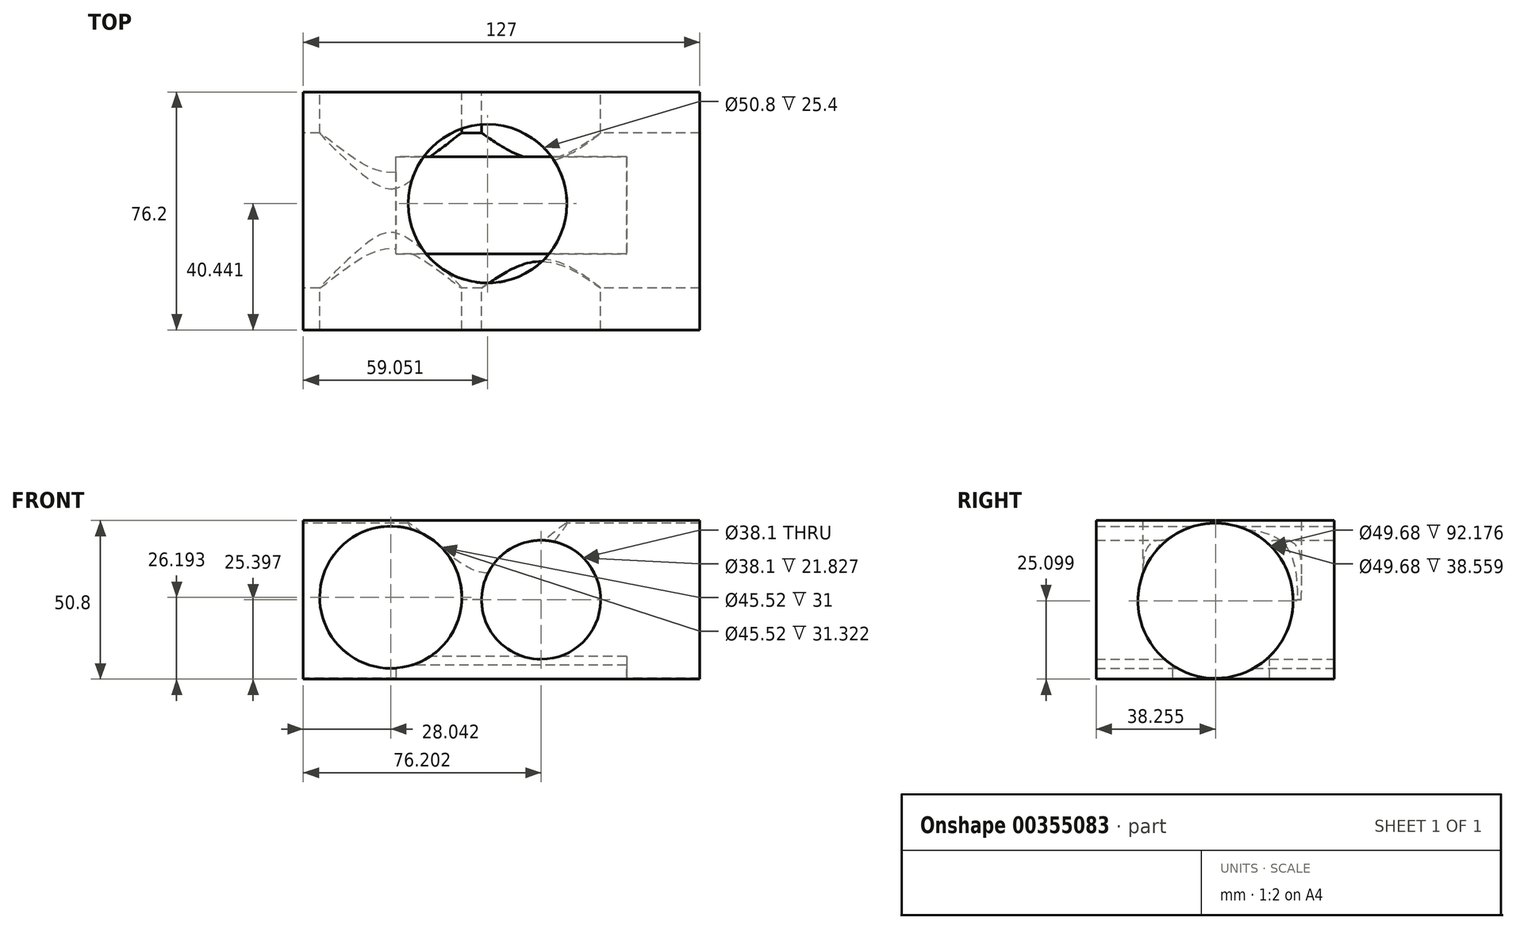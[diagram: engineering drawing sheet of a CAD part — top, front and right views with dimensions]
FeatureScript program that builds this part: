
annotation { "Feature Type Name" : "Feature", "Feature Type Description" : "" }
export const myFeature = defineFeature(function(context is Context, id is Id, definition is map)
    precondition{}
    {
        {
            var Q0;
            Q0=qCreatedBy(makeId("Front.planeOp"),FACE);
            var sketch = newSketch(context, id + "F0", { "sketchPlane" : qUnion([Q0])});
            skLineSegment(sketch, "E0.bottom", {"start": v(-45.49, 55.88) * mm, "end": v(81.51, 55.88) * mm});
            skLineSegment(sketch, "E0.top", {"start": v(-45.49, 5.08) * mm, "end": v(81.51, 5.08) * mm});
            skLineSegment(sketch, "E0.left", {"start": v(-45.49, 55.88) * mm, "end": v(-45.49, 5.08) * mm});
            skLineSegment(sketch, "E0.right", {"start": v(81.51, 55.88) * mm, "end": v(81.51, 5.08) * mm});
            skCircle(sketch, "E1", {"center": v(30.71, 30.48) * mm, "radius": 19.05 * mm});
            skSolve(sketch);
        }
        {
            var Q0;
            Q0=makeQuery(id+"F0.imprint","IMPRINT",FACE,{"disambiguationData":[TD([[makeQuery(id+"F0.imprint","IMPRINT",EDGE,{"derivedFrom":sQuery(id+"F0.wireOp",EDGE,"E0.bottom")}),-1.0]])]});
            extrude(context, id + "F1", {"entities" : qUnion([Q0]), "depth" : 76.2 * mm});
        }
        {
            var Q0;
            Q0=makeQuery(id+"F1.opExtrude","SWEPT_FACE",FACE,{"disambiguationData":[OSD([sQuery(id+"F0.wireOp",EDGE,"E0.bottom")])]});
            var sketch = newSketch(context, id + "F2", { "sketchPlane" : qUnion([Q0])});
            skCircle(sketch, "E2", {"center": v(13.56, -35.76) * mm, "radius": 25.4 * mm});
            skSolve(sketch);
        }
        {
            var Q0;
            Q0=makeQuery(id+"F2.imprint","IMPRINT",FACE,{"disambiguationData":[TD([[makeQuery(id+"F2.imprint","IMPRINT",EDGE,{"derivedFrom":sQuery(id+"F2.wireOp",EDGE,"E2")}),1.0]])]});
            extrude(context, id + "F3", {"entities" : qUnion([Q0]), "operationType" : NewBodyOperationType.REMOVE, "oppositeDirection" : true, "depth" : 25.4 * mm});
        }
        {
            var Q0;
            Q0=makeQuery(id+"F1.opExtrude","SWEPT_FACE",FACE,{"disambiguationData":[OSD([sQuery(id+"F0.wireOp",EDGE,"E0.top")])]});
            var sketch = newSketch(context, id + "F4", { "sketchPlane" : qUnion([Q0])});
            skLineSegment(sketch, "E3.bottom", {"start": v(-15.82, 51.78) * mm, "end": v(58.1, 51.78) * mm});
            skLineSegment(sketch, "E3.top", {"start": v(-15.82, 20.71) * mm, "end": v(58.1, 20.71) * mm});
            skLineSegment(sketch, "E3.left", {"start": v(-15.82, 51.78) * mm, "end": v(-15.82, 20.71) * mm});
            skLineSegment(sketch, "E3.right", {"start": v(58.1, 51.78) * mm, "end": v(58.1, 20.71) * mm});
            skSolve(sketch);
        }
        {
            var Q0;
            Q0=makeQuery(id+"F4.imprint","IMPRINT",FACE,{"disambiguationData":[TD([[makeQuery(id+"F4.imprint","IMPRINT",EDGE,{"derivedFrom":sQuery(id+"F4.wireOp",EDGE,"E3.bottom")}),-1.0]])]});
            extrude(context, id + "F5", {"entities" : qUnion([Q0]), "operationType" : NewBodyOperationType.REMOVE, "oppositeDirection" : true, "depth" : 25.4 * mm});
        }
        {
            var Q0;
            Q0=makeQuery(id+"F1.opExtrude","SWEPT_FACE",FACE,{"disambiguationData":[OSD([sQuery(id+"F0.wireOp",EDGE,"E0.left")])]});
            var sketch = newSketch(context, id + "F6", { "sketchPlane" : qUnion([Q0])});
            skCircle(sketch, "E4", {"center": v(37.94, 30.18) * mm, "radius": 24.84 * mm});
            skSolve(sketch);
        }
        {
            var Q0;
            Q0 = qSketchRegion(id + "F6", true);
            extrude(context, id + "F7", {"entities" : qUnion([Q0]), "operationType" : NewBodyOperationType.REMOVE, "oppositeDirection" : true, "depth" : 228.6 * mm});
        }
        {
            var Q0;
            Q0=makeQuery(id+"F1.opExtrude","CAP_FACE",FACE,{"disambiguationData":[OSD([sQuery(id+"F0.wireOp",EDGE,"E0.bottom"),sQuery(id+"F0.wireOp",EDGE,"E0.top"),sQuery(id+"F0.wireOp",EDGE,"E0.left"),sQuery(id+"F0.wireOp",EDGE,"E0.right"),sQuery(id+"F0.wireOp",EDGE,"E1")])],"isStart":true});
            var sketch = newSketch(context, id + "F8", { "sketchPlane" : qUnion([Q0])});
            skCircle(sketch, "E5", {"center": v(17.45, 31.27) * mm, "radius": 22.76 * mm});
            skSolve(sketch);
        }
        {
            var Q0;
            Q0=makeQuery(id+"F8.imprint","IMPRINT",FACE,{"disambiguationData":[TD([[makeQuery(id+"F8.imprint","IMPRINT",EDGE,{"derivedFrom":sQuery(id+"F8.wireOp",EDGE,"E5")}),1.0]])]});
            extrude(context, id + "F9", {"entities" : qUnion([Q0]), "operationType" : NewBodyOperationType.REMOVE, "oppositeDirection" : true, "depth" : 228.6 * mm});
        }
    });
